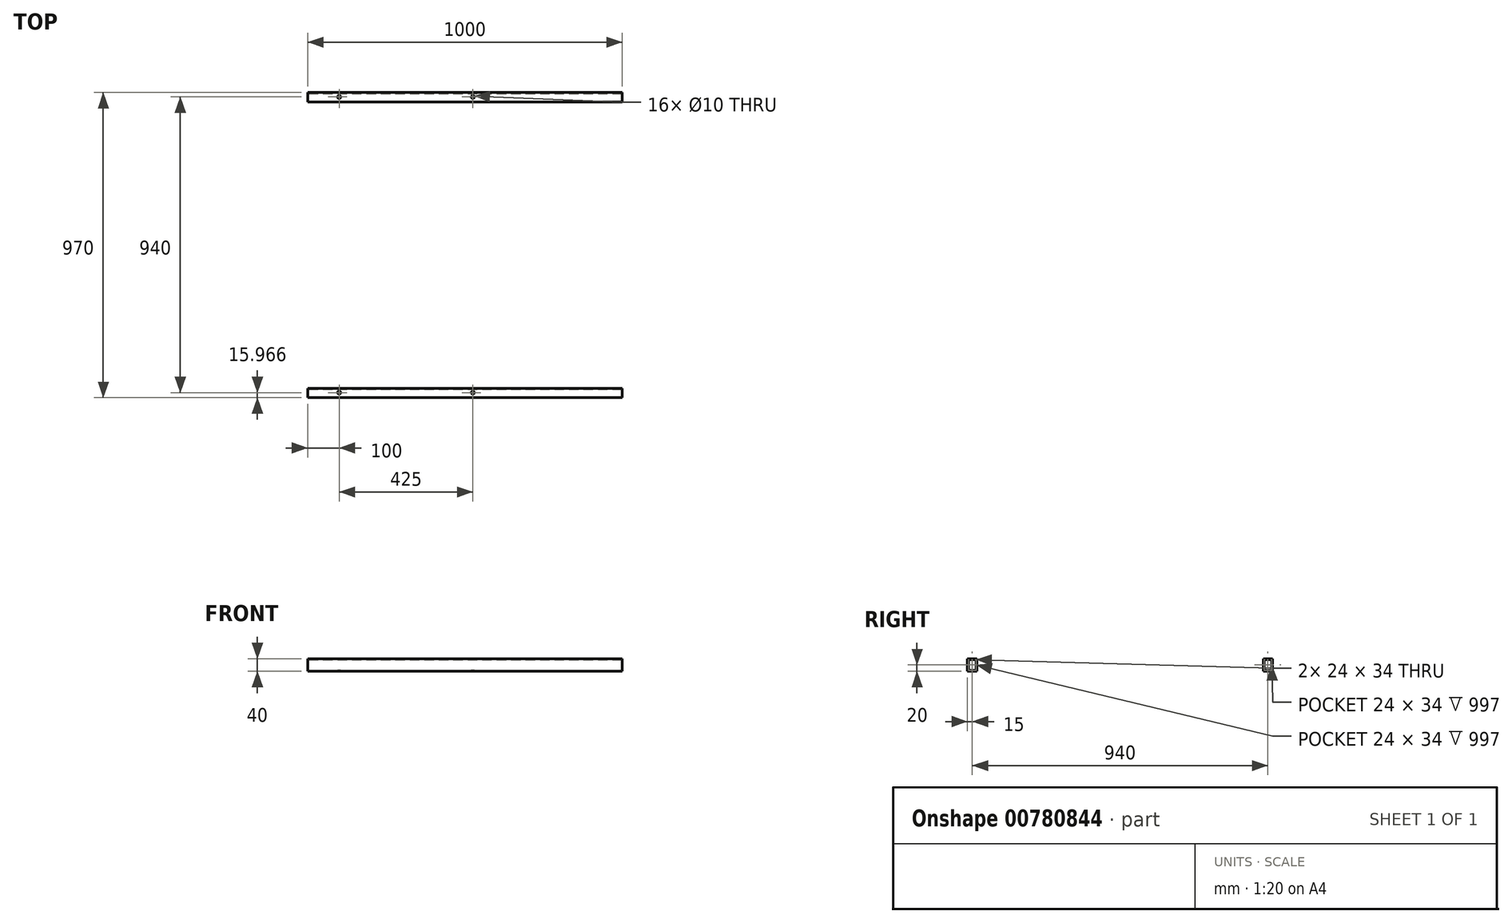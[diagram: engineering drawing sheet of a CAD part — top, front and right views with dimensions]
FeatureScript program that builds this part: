
annotation { "Feature Type Name" : "Feature", "Feature Type Description" : "" }
export const myFeature = defineFeature(function(context is Context, id is Id, definition is map)
    precondition{}
    {
        {
            var Q0;
            Q0=qCreatedBy(makeId("Front.planeOp"),FACE);
            var sketch = newSketch(context, id + "F0", { "sketchPlane" : qUnion([Q0])});
            skLineSegment(sketch, "E0.bottom", {"start": v(-500, -20) * mm, "end": v(500, -20) * mm});
            skLineSegment(sketch, "E0.top", {"start": v(-500, 20) * mm, "end": v(500, 20) * mm});
            skLineSegment(sketch, "E0.left", {"start": v(-500, -20) * mm, "end": v(-500, 20) * mm});
            skLineSegment(sketch, "E0.right", {"start": v(500, -20) * mm, "end": v(500, 20) * mm});
            skPoint(sketch, "E0.middle", {"position": v(0, 0) * mm});
            skPoint(sketch, "E1.positionSnap0", {"position": v(-500, 0) * mm});
            skPoint(sketch, "E2", {"position": v(-500, -20) * mm});
            skPoint(sketch, "E3", {"position": v(-475, -5) * mm});
            skPoint(sketch, "E4", {"position": v(-430, -5) * mm});
            skPoint(sketch, "E5", {"position": v(-160, -5) * mm});
            skSolve(sketch);
        }
        {
            var Q0;
            Q0 = qSketchRegion(id + "F0", true);
            extrude(context, id + "F1", {"entities" : qUnion([Q0]), "depth" : 30 * mm, "offsetDistance" : 25 * mm});
        }
        {
            var Q0;
            Q0=makeQuery(id+"F1.opExtrude","SWEPT_FACE",FACE,{"disambiguationData":[OSD([sQuery(id+"F0.wireOp",EDGE,"E0.right")])]});
            shell(context, id + "F2", {"entities" : qUnion([Q0]), "thickness" : 3 * mm});
        }
        {
            var Q0;
            Q0=makeQuery(id+"F1.opExtrude","SWEPT_FACE",FACE,{"disambiguationData":[OSD([sQuery(id+"F0.wireOp",EDGE,"E0.top")])]});
            var sketch = newSketch(context, id + "F3", { "sketchPlane" : qUnion([Q0])});
            skPoint(sketch, "E6", {"position": v(-400, -14.03) * mm});
            skPoint(sketch, "E7", {"position": v(25, -14.03) * mm});
            skSolve(sketch);
        }
        {
            var Q0;
            Q0=sQuery(id+"F3.wireOp",VERTEX,"E6");
            var Q1;
            Q1=sQuery(id+"F3.wireOp",VERTEX,"E7");
            var Q2;
            Q2=makeQuery(id+"F1.opExtrude","SWEPT_BODY",BODY,{"disambiguationData":[OSD([sQuery(id+"F0.wireOp",EDGE,"E0.bottom"),sQuery(id+"F0.wireOp",EDGE,"E0.top"),sQuery(id+"F0.wireOp",EDGE,"E0.left"),sQuery(id+"F0.wireOp",EDGE,"E0.right")])]});
            hole(context, id + "F4", {"style" : HoleStyle.SIMPLE, "endStyle" : HoleEndStyle.THROUGH, "holeDiameter" : 10 * mm, "majorDiameter" : 5 * mm, "isTappedThrough" : true, "tappedDepth" : 12 * mm, "tapClearance" : 3, "locations" : qUnion([Q0, Q1]), "scope" : qUnion([Q2])});
        }
        {
            var Q0;
            Q0=makeQuery(id+"F1.opExtrude","SWEPT_BODY",BODY,{"disambiguationData":[OSD([sQuery(id+"F0.wireOp",EDGE,"E0.bottom"),sQuery(id+"F0.wireOp",EDGE,"E0.top"),sQuery(id+"F0.wireOp",EDGE,"E0.left"),sQuery(id+"F0.wireOp",EDGE,"E0.right")])]});
            transform(context, id + "F5", {"entities" : qUnion([Q0]), "transformType" : TransformType.TRANSLATION_3D, "dx" : 0 * mm, "dy" : 940 * mm, "dz" : 0 * mm, "makeCopy" : true});
        }
    });
